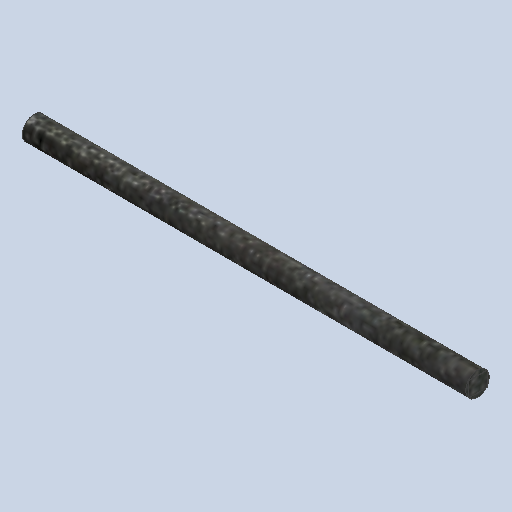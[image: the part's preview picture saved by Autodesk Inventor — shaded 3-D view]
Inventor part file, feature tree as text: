
AUTODESK INVENTOR PART (.ipt)
format: ipt  version: 2024.3 (Build 283343000, 343)  size: 247,296 bytes
history: native  units: mm
features: extrude x2, sketch x2
ambient origin geometry x8: Origin, YZ Plane, XZ Plane, XY Plane, X Axis, Y Axis, Z Axis, Center Point
bodies: Solid1 (feature_tree)
feature tree (4):
  extrude  "Extrusion1"  Depth=94.0mm TaperAngle=0.0deg
  extrude  "Extrusion2"  [1 undecoded]
  sketch  "Sketch1"  dims[d0=5.0mm d1=94.0mm d2=0.0mm]
  sketch  "Sketch2"  dims[d3=0.1mm d4=0.0mm]
note: 1 required parameter value undecoded (feature->parameter linkage not recoverable at this tier; creation-order binding heuristic only, values carry confidence <= 0.55)
